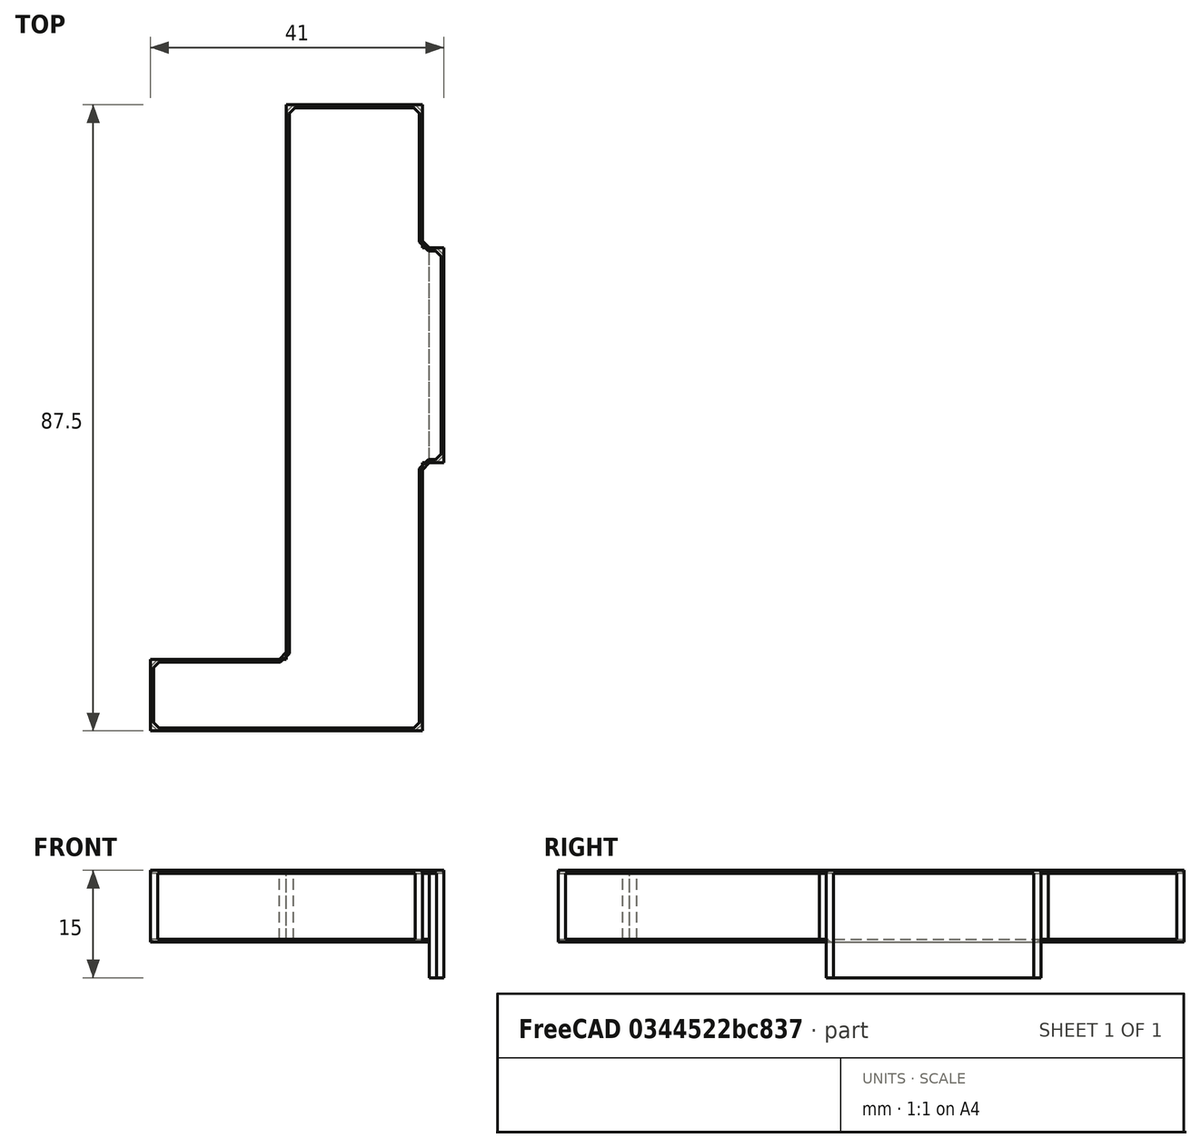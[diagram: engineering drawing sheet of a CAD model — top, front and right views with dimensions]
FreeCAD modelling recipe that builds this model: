
FCSTD DOCUMENT  (FreeCAD 0.18R14555 (Git shallow))
Label: loli-bear-Z-aligner
License: All rights reserved
LicenseURL: http://en.wikipedia.org/wiki/All_rights_reserved
objects: Part::Box×4, Part::Chamfer×2, Part::MultiFuse×1, Part::Feature×1
note: 8 computed .brp shape members not serialized (recipe doc carries the construction recipe); baked Part::Feature solids carry a one-line shape summary decoded from their .brp

FEATURE [Part::Box] Box001  label="Cube001"
  AttacherType = Attacher::AttachEngine3D
  Height = 10
  Length = 38
  Placement = pos=(-9,-77.5,0) rot=(0,0,1;0rad)
  Width = 10
FEATURE [Part::Box] Box002  label="Cube002"
  AttacherType = Attacher::AttachEngine3D
  Height = 10
  Length = 19
  Placement = pos=(10,-71,0) rot=(0,0,1;0rad)
  Width = 81
FEATURE [Part::Box] Box003  label="Cube003"
  AttacherType = Attacher::AttachEngine3D
  Height = 10
  Length = 3
  Placement = pos=(29,-40,0) rot=(0,0,1;0rad)
  Width = 30
FEATURE [Part::Box] Box004  label="Cube004"
  AttacherType = Attacher::AttachEngine3D
  Height = 5
  Length = 2
  Placement = pos=(30,-40,-5) rot=(0,0,1;0rad)
  Width = 30
FEATURE [Part::MultiFuse] Fusion
  Shapes = -> [Box003,Box002,Box001,Box004]
FEATURE [Part::Feature] Fusion001
  shape: bbox 41 x 87.5 x 15 mm, 14 faces (baked)
FEATURE [Part::Chamfer] Chamfer
  Base = -> Fusion001
  Edges = 10 edges r=1: [Edge2,Edge4,Edge6,Edge9,Edge11,Edge14,Edge17,Edge31,Edge32,Edge34]
FEATURE [Part::Chamfer] Chamfer001
  Base = -> Chamfer
  Edges = 35 edges r=0.4: [Edge1,Edge4,Edge5,Edge6,Edge7,Edge9,Edge10,Edge11,Edge12,Edge13,Edge14,Edge15,Edge16,Edge17,Edge18,Edge19,Edge21,Edge23,Edge24,Edge25,Edge26,Edge27,Edge28,Edge29,Edge30,Edge31,Edge32,Edge33,Edge34,Edge35,Edge36,Edge37,Edge38,Edge39,Edge40]
